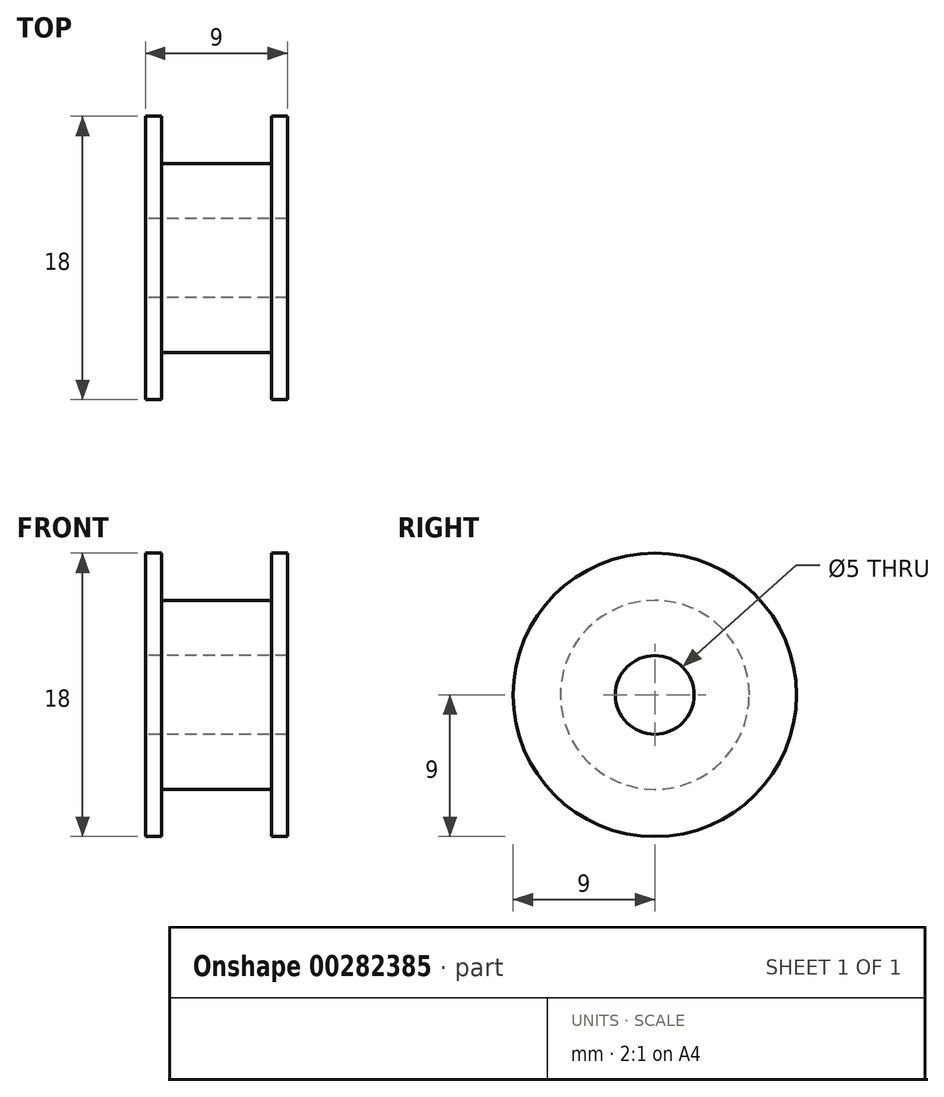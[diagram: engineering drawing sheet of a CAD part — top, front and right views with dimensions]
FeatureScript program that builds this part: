
annotation { "Feature Type Name" : "Feature", "Feature Type Description" : "" }
export const myFeature = defineFeature(function(context is Context, id is Id, definition is map)
    precondition{}
    {
        {
            var Q0;
            Q0=qCreatedBy(makeId("Top.planeOp"),FACE);
            var sketch = newSketch(context, id + "F0", { "sketchPlane" : qUnion([Q0])});
            skLineSegment(sketch, "E0", {"start": v(0, 0) * mm, "end": v(0, 9) * mm});
            skLineSegment(sketch, "E1", {"start": v(0, 9) * mm, "end": v(1, 9) * mm});
            skLineSegment(sketch, "E2", {"start": v(1, 9) * mm, "end": v(1, 6) * mm});
            skLineSegment(sketch, "E3", {"start": v(1, 6) * mm, "end": v(8, 6) * mm});
            skLineSegment(sketch, "E4", {"start": v(8, 6) * mm, "end": v(8, 9) * mm});
            skLineSegment(sketch, "E5", {"start": v(8, 9) * mm, "end": v(9, 9) * mm});
            skLineSegment(sketch, "E6", {"start": v(9, 9) * mm, "end": v(9, 0) * mm});
            skLineSegment(sketch, "E7", {"start": v(9, 0) * mm, "end": v(0, 0) * mm});
            skSolve(sketch);
        }
        {
            var Q0;
            Q0=qSketchRegion(id+"F0",true);
            var Q1;
            Q1=sQuery(id+"F0.wireOp",EDGE,"E7");
            revolve(context, id + "F1", {"entities" : qUnion([Q0]), "axis" : qUnion([Q1]), "revolveType" : RevolveType.FULL});
        }
        {
            var Q0;
            Q0=makeQuery(id+"F1.opRevolve","SWEPT_FACE",FACE,{"disambiguationData":[OSD([sQuery(id+"F0.wireOp",EDGE,"E0")])]});
            var sketch = newSketch(context, id + "F2", { "sketchPlane" : qUnion([Q0])});
            skCircle(sketch, "E8", {"center": v(0, 0) * mm, "radius": 2.5 * mm});
            skSolve(sketch);
        }
        {
            var Q0;
            Q0=qSketchRegion(id+"F2",true);
            extrude(context, id + "F3", {"entities" : qUnion([Q0]), "operationType" : NewBodyOperationType.REMOVE, "oppositeDirection" : true, "depth" : 25 * mm});
        }
    });
